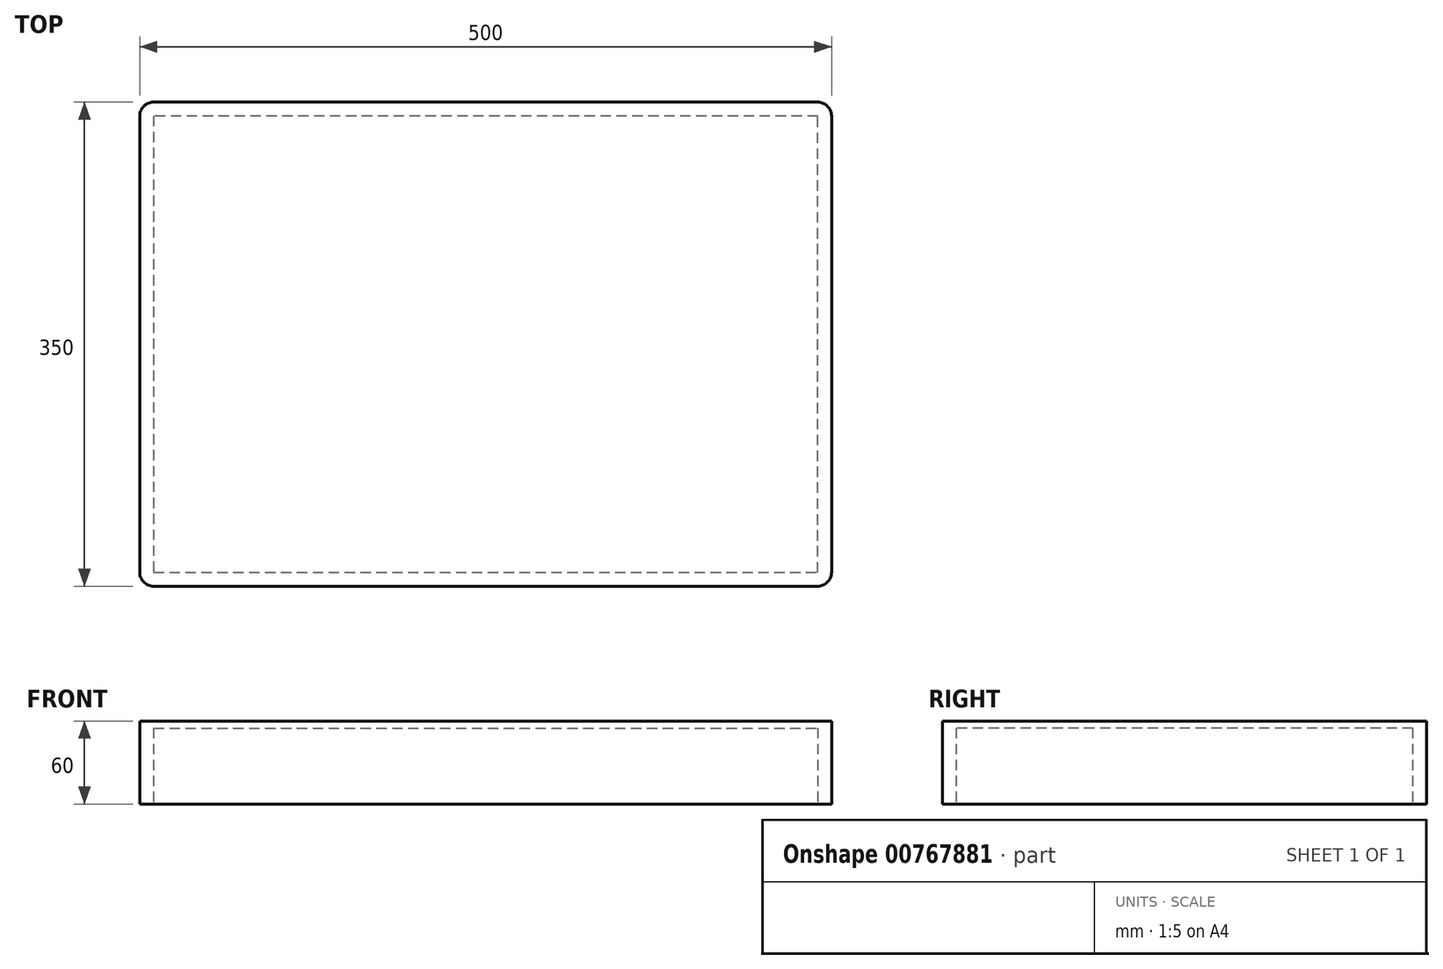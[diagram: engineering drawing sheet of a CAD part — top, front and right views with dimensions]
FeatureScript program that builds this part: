
annotation { "Feature Type Name" : "Feature", "Feature Type Description" : "" }
export const myFeature = defineFeature(function(context is Context, id is Id, definition is map)
    precondition{}
    {
        {
            var Q0;
            Q0=qCreatedBy(makeId("Top.planeOp"),FACE);
            var sketch = newSketch(context, id + "F0", { "sketchPlane" : qUnion([Q0])});
            skLineSegment(sketch, "E0.bottom", {"start": v(240, 175) * mm, "end": v(-240, 175) * mm});
            skLineSegment(sketch, "E0.top", {"start": v(240, -175) * mm, "end": v(-240, -175) * mm});
            skLineSegment(sketch, "E0.left", {"start": v(250, 165) * mm, "end": v(250, -165) * mm});
            skLineSegment(sketch, "E0.right", {"start": v(-250, 165) * mm, "end": v(-250, -165) * mm});
            skPoint(sketch, "E0.middle", {"position": v(0, 0) * mm});
            skPoint(sketch, "E1.visualSharp", {"position": v(-250, 175) * mm});
            skPoint(sketch, "E2.visualSharp", {"position": v(250, 175) * mm});
            skPoint(sketch, "E3.visualSharp", {"position": v(250, -175) * mm});
            skPoint(sketch, "E4.visualSharp", {"position": v(-250, -175) * mm});
            skArc(sketch, "E5.filletArc", {"start": v(-240, 175) * mm, "mid": v(-247.07, 172.07) * mm, "end": v(-250, 165) * mm});
            skArc(sketch, "E6.filletArc", {"start": v(-250, -165) * mm, "mid": v(-247.07, -172.07) * mm, "end": v(-240, -175) * mm});
            skArc(sketch, "E7.filletArc", {"start": v(240, -175) * mm, "mid": v(247.07, -172.07) * mm, "end": v(250, -165) * mm});
            skArc(sketch, "E8.filletArc", {"start": v(250, 165) * mm, "mid": v(247.07, 172.07) * mm, "end": v(240, 175) * mm});
            skSolve(sketch);
        }
        {
            var Q0;
            Q0=makeQuery(id+"F0.imprint","IMPRINT",FACE,{"disambiguationData":[TD([[makeQuery(id+"F0.imprint","IMPRINT",EDGE,{"derivedFrom":sQuery(id+"F0.wireOp",EDGE,"E0.bottom")}),1.0]])]});
            extrude(context, id + "F1", {"entities" : qUnion([Q0]), "depth" : 60 * mm, "offsetDistance" : 25 * mm});
        }
        {
            var Q0;
            Q0=makeQuery(id+"F0.imprint","IMPRINT",FACE,{"disambiguationData":[TD([[makeQuery(id+"F0.imprint","IMPRINT",EDGE,{"derivedFrom":sQuery(id+"F0.wireOp",EDGE,"E0.bottom")}),1.0]])]});
            var sketch = newSketch(context, id + "F2", { "sketchPlane" : qUnion([Q0])});
            skLineSegment(sketch, "E9.0", {"start": v(-240, -165) * mm, "end": v(240, -165) * mm});
            skLineSegment(sketch, "E9.1", {"start": v(-240, 165) * mm, "end": v(-240, -165) * mm});
            skLineSegment(sketch, "E9.2", {"start": v(240, 165) * mm, "end": v(-240, 165) * mm});
            skLineSegment(sketch, "E9.3", {"start": v(240, -165) * mm, "end": v(240, 165) * mm});
            skSolve(sketch);
        }
        {
            var Q0;
            Q0=makeQuery(id+"F2.imprint","IMPRINT",FACE,{"disambiguationData":[TD([[makeQuery(id+"F2.imprint","IMPRINT",EDGE,{"derivedFrom":sQuery(id+"F2.wireOp",EDGE,"E9.0")}),1.0]])]});
            extrude(context, id + "F3", {"entities" : qUnion([Q0]), "operationType" : NewBodyOperationType.REMOVE, "depth" : 55 * mm, "offsetDistance" : 25 * mm});
        }
    });
